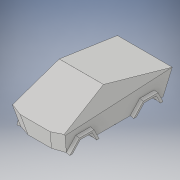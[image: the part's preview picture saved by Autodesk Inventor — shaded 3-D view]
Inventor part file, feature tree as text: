
AUTODESK INVENTOR PART (.ipt)
format: ipt  version: 2018 (Build 220112000, 112)  size: 244,736 bytes
history: native  units: in
note: dims shown in document units (in); Inventor stores cm internally (conversion verified against a paired STEP export)
features: chamfer x11, extrude x6, sketch x6, other x2
ambient origin geometry x8: Origin, YZ Plane, XZ Plane, XY Plane, X Axis, Y Axis, Z Axis, Center Point
bodies: Solid1 (feature_tree)
feature tree (25):
  other  "Annotations"
  extrude  "Extrusion1"  Depth=3.0in
  chamfer  "Chamfer1"  Distance=0.7in
  chamfer  "Chamfer2"  Distance=0.7in Angle=45.0deg
  chamfer  "Chamfer3"  Distance=0.7in Angle=45.0deg
  chamfer  "Chamfer4"  Distance=0.7in Angle=45.0deg
  extrude  "Extrusion2"  Depth=0.1in
  extrude  "Extrusion3"  Depth=0.4in
  extrude  "Extrusion4"  Depth=0.4in
  extrude  "Extrusion5"  Depth=0.1in
  chamfer  "Chamfer9"  Angle=60.0deg  [1 undecoded]
  extrude  "Extrusion7"  Depth=0.1in
  chamfer  "Chamfer10"  Distance=0.1in
  chamfer  "Chamfer11"  Distance=0.1in
  chamfer  "Chamfer12"  Distance=0.8in
  chamfer  "Chamfer13"  Distance=0.4in
  chamfer  "Chamfer14"  Angle=60.0deg  [1 undecoded]
  chamfer  "Chamfer15"  Distance=0.4in
  sketch  "Sketch1"  dims[d0=1.5in d1=3.0in d2=0.7in d3=0.0in d4=0.7in d5=0.125in d6=45.0deg d7=0.7in d8=0.125in d9=45.0deg d10=0.7in d11=0.125in d12=45.0deg]
  sketch  "Sketch2"  dims[d13=0.5in d14=0.125in d15=45.0deg d16=0.1in]
  sketch  "Sketch3"  dims[d17=0.8in d18=0.4in]
  sketch  "Sketch4"  dims[d19=60.0deg d20=0.4in]
  sketch  "Sketch5"  dims[d21=0.1in d22=0.8in]
  sketch  "Sketch9"  dims[d23=0.4in d24=60.0deg d25=0.4in d26=0.1in d27=0.0in d28=0.1in d29=0.8in d30=0.4in d31=60.0deg d32=0.4in d33=0.1in d34=0.8in d35=0.4in d36=60.0deg d37=0.4in d38=0.1in d39=0.0in d40=0.4in d41=0.07in d42=0.4in d43=0.07in d44=0.3in d45=0.0in d46=0.4in d47=0.07in d48=0.4in d49=0.07in d50=0.3in d51=0.0in d66=3.0in d67=0.2in d68=45.0deg d69=0.5in d70=0.0in d71=0.125in d72=0.5in d73=45.0deg d74=0.125in d75=0.5in d76=45.0deg d77=1.3in d78=0.5in d79=45.0deg d83=1.706in d84=0.5in d85=45.0deg d99=0.3in d100=0.1in d101=45.0deg d102=0.3in d103=0.1in d104=45.0deg d108=0.1833in d109=0.2196in d110=1.25in]
  other  "Linear Dimension 2"
note: 2 required parameter values undecoded (feature->parameter linkage not recoverable at this tier; creation-order binding heuristic only, values carry confidence <= 0.55)
